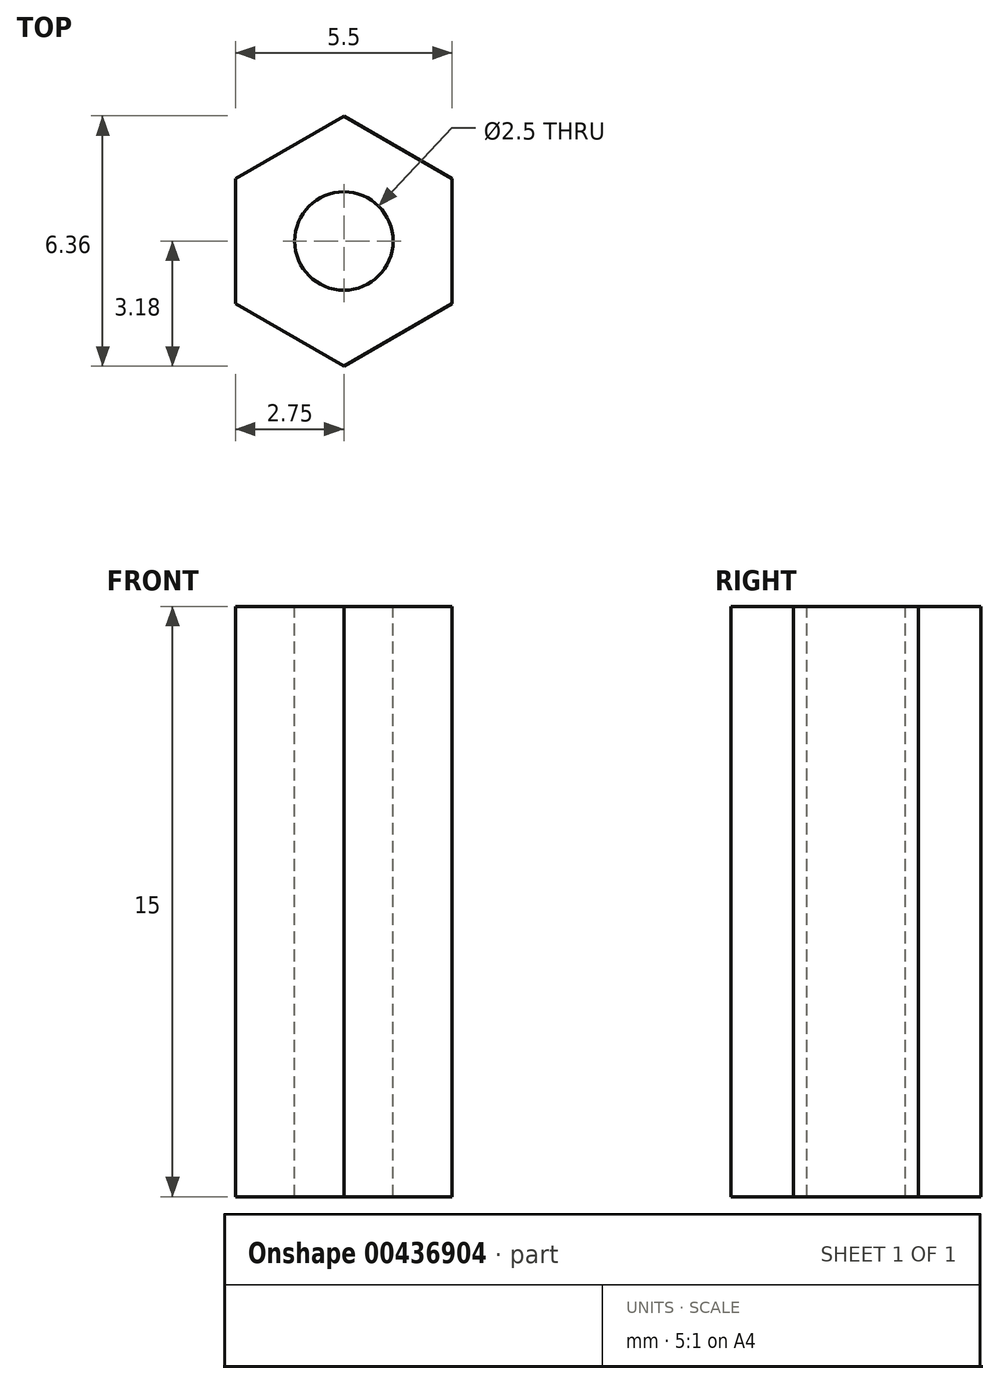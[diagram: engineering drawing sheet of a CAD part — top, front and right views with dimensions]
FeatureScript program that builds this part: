
annotation { "Feature Type Name" : "Feature", "Feature Type Description" : "" }
export const myFeature = defineFeature(function(context is Context, id is Id, definition is map)
    precondition{}
    {
        {
            var Q0;
            Q0=qCreatedBy(makeId("Top.planeOp"),FACE);
            var sketch = newSketch(context, id + "F0", { "sketchPlane" : qUnion([Q0])});
            skCircle(sketch, "E0.cCircle", {"center": v(0, 0) * mm, "radius": 2.75 * mm, "construction": true});
            skLineSegment(sketch, "E0.0", {"start": v(2.75, 1.59) * mm, "end": v(2.75, -1.59) * mm});
            skLineSegment(sketch, "E0.1", {"start": v(2.75, -1.59) * mm, "end": v(0, -3.18) * mm});
            skLineSegment(sketch, "E0.2", {"start": v(0, -3.18) * mm, "end": v(-2.75, -1.59) * mm});
            skLineSegment(sketch, "E0.3", {"start": v(-2.75, -1.59) * mm, "end": v(-2.75, 1.59) * mm});
            skLineSegment(sketch, "E0.4", {"start": v(-2.75, 1.59) * mm, "end": v(0, 3.18) * mm});
            skLineSegment(sketch, "E0.5", {"start": v(0, 3.18) * mm, "end": v(2.75, 1.59) * mm});
            skPoint(sketch, "E0.0.midPoint", {"position": v(2.75, 0) * mm});
            skSolve(sketch);
        }
        {
            var Q0;
            Q0 = qSketchRegion(id + "F0", true);
            extrude(context, id + "F1", {"entities" : qUnion([Q0]), "depth" : 15 * mm});
        }
        {
            var Q0;
            Q0=makeQuery(id+"F1.opExtrude","CAP_FACE",FACE,{"disambiguationData":[OSD([sQuery(id+"F0.wireOp",EDGE,"E0.0"),sQuery(id+"F0.wireOp",EDGE,"E0.1"),sQuery(id+"F0.wireOp",EDGE,"E0.2"),sQuery(id+"F0.wireOp",EDGE,"E0.3"),sQuery(id+"F0.wireOp",EDGE,"E0.4"),sQuery(id+"F0.wireOp",EDGE,"E0.5")])],"isStart":false});
            var sketch = newSketch(context, id + "F2", { "sketchPlane" : qUnion([Q0])});
            skPoint(sketch, "E1", {"position": v(0, 0) * mm});
            skSolve(sketch);
        }
        {
            var Q0;
            Q0=sQuery(id+"F2.wireOp",VERTEX,"E1");
            var Q1;
            Q1=makeQuery(id+"F1.opExtrude","SWEPT_BODY",BODY,{"disambiguationData":[OSD([sQuery(id+"F0.wireOp",EDGE,"E0.0"),sQuery(id+"F0.wireOp",EDGE,"E0.1"),sQuery(id+"F0.wireOp",EDGE,"E0.2"),sQuery(id+"F0.wireOp",EDGE,"E0.3"),sQuery(id+"F0.wireOp",EDGE,"E0.4"),sQuery(id+"F0.wireOp",EDGE,"E0.5")])]});
            hole(context, id + "F3", {"style" : HoleStyle.SIMPLE, "endStyle" : HoleEndStyle.THROUGH, "standardTappedOrClearance" : lookupTablePath({ "standard" : "ISO", "engagement" : "75%", "pitch" : "0.5 mm", "size" : "M3", "type" : "Tapped" }), "standardBlindInLast" : lookupTablePath({ "standard" : "ISO", "engagement" : "75%", "pitch" : "0.5 mm", "size" : "M3", "type" : "Tapped" }), "holeDiameter" : 2.5 * mm, "showTappedDepth" : true, "isTappedThrough" : true, "tappedDepth" : 12 * mm, "tapClearance" : 3, "locations" : qUnion([Q0]), "scope" : qUnion([Q1]), "majorDiameter" : 3 * mm});
        }
    });
